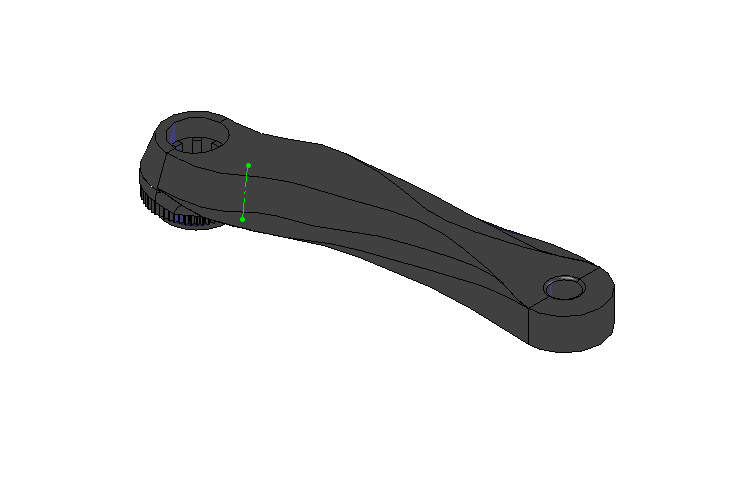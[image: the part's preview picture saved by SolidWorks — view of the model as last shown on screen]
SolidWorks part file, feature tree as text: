
SOLIDWORKS PART (.sldprt)
format: sldprt  version: not decoded by parser v0  size: 1,992,192 bytes
history: native  units: mm
features: sketch x33, plane x16, cut_extrude x4, revolve x2, fillet x2, pattern_circular x2, material x1, sweep x1, cut_revolve x1 (+10 scaffold rows collapsed)
feature tree (72):
  scaffold x10  (default folders/planes/origin — collapsed)
  material  "Matériau <non spécifié>"
  plane  "Plan de face"
  plane  "Plan de dessus"
  plane  "Plan de droite"
  plane  "Plan0"  Offset=0mm
  plane  "Plan17"  Offset=17mm
  plane  "Plan34"  Offset=34mm
  plane  "Plan51"  Offset=51mm
  plane  "Plan68"  Offset=68mm
  plane  "Plan85"  Offset=85mm
  plane  "Plan102"  Offset=102mm
  plane  "Plan119"  Offset=119mm
  plane  "Plan136"  Offset=136mm
  plane  "Plan153"  Offset=153mm
  plane  "Plan170"  Offset=170mm
  sketch  "Esquisse1"  dims[D1=30.0mm D2=32.0mm D3=38.0mm D4=44.0mm D5=47.0mm D6=49.0mm D7=50.0mm D8=51.0mm D9=52.0mm D10=53.0mm D11=54.0mm]
  sketch  "Esquisse2"  dims[D1=18.0mm D2=18.0mm D3=22.0mm D4=27.0mm D5=32.0mm D6=36.0mm D7=38.0mm D8=39.5mm D9=40.5mm D10=40.0mm D11=39.5mm]
  sketch  "Esquisse3"  dims[c1.D1=37.0mm c1.D2=42.0mm c1.D3=42.0mm c1.D4=42.0mm c1.D5=40.0mm c1.D6=38.0mm c1.D7=36.0mm c1.D8=34.0mm c1.D9=33.0mm c1.D10=33.0mm c1.D11=33.0mm c2.D2=39.5mm]
  sketch  "Esquisse4"  dims[D1=28.0mm D2=28.0mm D3=28.0mm D4=25.0mm D5=21.0mm D6=15.0mm D7=7.0mm D8=7.0mm D9=14.0mm D10=23.0mm D11=33.0mm D12=~178.970178mm]
  sketch  "Esquisse5"
  sketch  "Esquisse6"  dims[D1=11.0mm D2=11.0mm D3=9.0mm D4=8.0mm D5=6.0mm D6=1.5mm D7=3.0mm D8=2.0mm]
  sketch  "Esquisse7"  dims[D1=35.0mm D2=28.0mm D3=24.0mm D4=21.0mm D5=~14.673184mm]
  sketch  "Esquisse8"  dims[D1=0.0mm]
  sketch  "Esquisse9"  dims[D1=11.0mm]
  sketch  "Esquisse10"  dims[c1.D1=5.0mm c1.D2=0.1mm c2.D1=0.1mm]
  sketch  "Esquisse11"  dims[D1=0.1mm]
  sketch  "Esquisse12"  dims[D1=0.1mm]
  sketch  "Esquisse13"  dims[D1=0.1mm]
  sketch  "Esquisse14"  dims[D1=0.1mm]
  sketch  "Esquisse15"
  sketch  "Esquisse16"
  sketch  "Esquisse17"
  sketch  "Esquisse18"
  sketch  "Esquisse19"  dims[c1.D1=2.0mm c1.D2=~12.895463mm c2.D1=0.1mm]
  sketch  "Esquisse20"  dims[c1.D1=0.1mm c1.D2=0.1mm c2.D1=~2.574604mm c2.D2=3.0mm c3.D1=0.1mm c3.D2=0.1mm]
  sketch  "Esquisse23"  dims[c1.D1=95.0mm c1.D2=1.5mm c1.D3=8.0mm c2.D2=1.5mm c2.D4=142.0mm c2.D5=10.0mm c3.D2=30.0mm c3.D6=2.0mm c3.D7=50.0mm c3.D8=~8.48585mm c4.D2=30.0mm c4.D7=8.0mm]
  sketch  "Esquisse24"  dims[c1.D2=~30.618801mm c1.D3=30.0mm c1.D1=~12.058422mm c2.D1=90.0deg c2.D2=15.0mm c2.D4=~15.479283mm]
  sweep  "Enlèvement de matière-Balayage2"
  sketch  "Esquisse21"
  revolve  "Révolution1"  Angle=180deg
  sketch  "Esquisse22"  dims[c1.D1=12.5mm c1.D2=38.0mm c2.D1=12.5mm c2.D2=10.0mm c2.D3=39.0mm c3.D2=23.0mm c3.D4=28.0mm c4.D2=23.0mm c4.D5=28.0mm c4.D6=37.0mm]
  revolve  "Révolution2"  Angle=360deg
  plane  "Plan171"  Offset=30mm
  plane  "Plan172"  Offset=17.5mm
  sketch  "Esquisse32"  dims[D1=21.0mm]
  sketch  "Esquisse33"  dims[D1=48.0mm]
  sketch  "Esquisse34"
  sketch  "Esquisse35"
  fillet  "Congé3"  Radius=3mm
  sketch  "Esquisse38"  dims[D1=12.0mm]
  cut_extrude  "Enlèv. mat.-Extru.4"  [1 undecoded]
  fillet  "Congé4"  Radius=1mm
  sketch  "Esquisse39"  dims[c1.D1=21.5mm c1.D2=17.5mm c1.D3=21.6mm c1.D4=21.8mm c1.D5=10.0mm c2.D3=10.0005mm c3.D3=1.0deg c3.D6=20.0mm c3.D1=21.8mm c3.D2=~10.001523mm c4.D2=1.0deg c4.D3=10.0mm c4.D4=20.0mm c4.D5=17.5mm c4.D6=21.0mm c5.D2=17.0mm c5.D5=~10.001523mm c6.D5=1.0deg]
  cut_revolve  "Enlèvement de matière-Révolution1"  Angle=360deg
  sketch  "Esquisse40"  dims[c1.D2=21.6mm c1.D1=3.0mm c1.D3=~17.315298mm c2.D3=22.5deg c2.D1=~3.63188mm]
  cut_extrude  "Enlèv. mat.-Extru.5"  [1 undecoded]
  pattern_circular  "Répétition circulaire1"  Count=8 Angle=45deg
  sketch  "Esquisse41"  dims[D1=37.0mm]
  cut_extrude  "Enlèv. mat.-Extru.6"  Depth=6mm
  sketch  "Esquisse42"  dims[c1.D1=33.0mm c1.D2=16.5mm c1.D3=33.0mm c2.D1=33.0mm c2.D2=33.0mm c2.D3=16.5mm c3.D1=~5.03863mm c3.D2=~1.496584mm c4.D2=45.0deg c4.D1=33.0mm c4.D3=~23.575068mm c5.D3=3.0deg c5.D4=~27.224326mm c6.D4=3.0deg c6.D5=0.2mm c6.D6=0.2mm c7.D5=~2.017411mm c8.D5=~36.419136deg c8.D1=0.2mm c8.D2=0.2mm c9.D1=~1.978948mm c10.D1=42.42deg c10.D2=~1.973201mm c11.D2=42.42deg c11.D3=0.2mm]
  cut_extrude  "Enlèv. mat.-Extru.7"  [1 undecoded]
  pattern_circular  "Répétition circulaire2"  Count=60 Angle=6deg
decode coverage: 33 of 45 modeling features carry decoded parameters
note: ~ marks probable driven/reference dimensions
note: 3 parameter values undecoded
summary: no parameter record found for 3 features
note: suppression state not decoded; provenance and decode notes live in map.json
